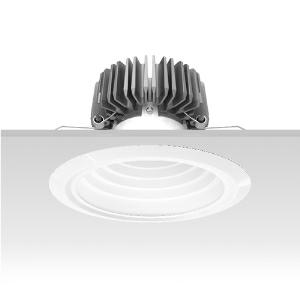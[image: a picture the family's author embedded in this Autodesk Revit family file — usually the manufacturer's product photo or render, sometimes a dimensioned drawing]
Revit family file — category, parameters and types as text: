
# Revit family: 3f_filippi_-_3f_reno_bianco_ampio_3f_filippi_-_30621_a01025_-_3f_reno_200_wh_2000-840_wide___vt_wh_48a5
name_source: partatom
category: Lighting Fixtures
units: mm (PartAtom-declared; Revit-internal decimal feet)

## family parameters
Cut with Voids When Loaded = No
Host = Face
Light Source = No
Part Type = Normal
Room Calculation Point = No
Round Connector Dimension = Use Diameter
Shared = No

## types (1)
- 3F Filippi - 3F Reno Bianco Ampio (1 x LED, 1884 lm, 20 W, 4000 K)
    Apparent Load = 20 VA
    Approval mark = CE
    CIE Flux Codes = 75 94 99 100 100
    Color Rendering = 80
    Color Temperature = 4000 K
    Control Gear = Electronic ballast
    Default Elevation = 1800 mm
    Description = ILLUMINOTECHNICAL
Luminous efficiency 100% (DLOR 100%, ULOR 0%).
Initial luminous flux of the luminaire 1884 lm.
Direct symmetric wide distribution.
Installation Interdistance Transv.D = 1.56 x hu - Long.D = 1.56 x hu.
Average luminance <3000 cd/m² for radial angles >65°.
Tabular UGR (CIE 117 - 4H-8H; S=0.25H; 70/50/20): RUG 20.8 - 20.6.
Beam angle: 74° - 74°.
Luminous efficacy 94 lm/W.
Lifetime (L90/B10): 30000 h. (tq+25°C)
Lifetime (L85/B10): 50000 h. (tq+25°C)
Lifetime (L70/B10): 80000 h. (tq+25°C)
Sudden decreased luminous flux after 50000 hours: 0% (C0).
Photobiological safety in compliance with IEC/TR 62778: RG0 risk exempt, (IEC 62471).
In compliance with IEC/EN 62722-2-1 - IEC/EN 62717 standards.

SOURCE
Compact LED module 2000/840.
Energy efficiency class (UE 2019/2020 - UE 2019/2015): D.
CIE 13.3 Colour rendering index: CRI >80 (R9 <50%).
IES TM-30 Fidelity Index: Rf = 84 Rg = 95.
CCT nominal colour temperature 4000 K.
Colour initial tolerance (MacAdam): SDCM 3.
Zhaga Book 3 compliant.

MECHANICAL
Passive heat dissipator in die-casting aluminium, oversized, for optimum thermal management of the LED module.
Parabolic element with graduated/concentric rings in white polycarbonate.
Transparent external lens with glossy and satin differentiated surfaces, with a cooling and anti-insect system in methacrylate (PMMA).
Fastening spring clips in stainless steel.
Dimensions: diameter 226 mm, height 146 mm. Weight 1.06 kg.
IP44 protection degree for exposed part, IP20 for recessed part.
Mechanical strength to impacts IK06 (1 joule).
Glow-wire test resistance 650°C.

ELECTRICAL
Wiring on a separate unit.
Halogen Free electronic wiring 230V-50/60Hz, power factor 0.95, THD <25%, constant output current, SELV, class II, 1 driver.
Power of the luminaire 20 W.
ENEC - CE.
SAFE FLICKER: PstLM=<1 and SVM=<0.4 (IEC TR 61547-1 and IEC TR 63158), to ensure a more comfortable and safe light.
Luminaire compliant with EN 60598-2-22 for power supply from a centralised emergency system CPSS (Central Power Supply System), not incorporated in the luminaire - high risk areas excluded. The default power and flux are 100% in AC and 100% in DC.
Ambient temperature from 0°C to +25°C.
Temperature class T6 max 85°C.
Relative humidity UR: <85%.

INSTALLATION
Pull-up recessed fitting.
False ceiling carving: 200 mm.
All accessories dedicated to this product are available on the Catalog and on our website www.3F-Filippi.com.

ACCESSORIES
A01025 - VT transparent glass, tempered, not flammable, locked and in line with the trim, in white polycarbonate.

APPLICATIONS
Environments: architectural, commercial, exhibition areas, transit areas, corridors, shops, display windows, service areas.
In false ceilings with narrow voids.

WARNING
Luminaire designed for disposal/recycling at end-of-life.
Replaceable (LED only) light source by a professional. Replaceable control gear by a professional.
    Height = 0 mm  [stored 0 ft]
    Lamp = 1 x LED
    Lamp Light Flux = 1884 lm
    Lamp Power = 20 W
    Lamp count = 1
    Length = 226 mm
    Lifetime = 50000 h
    Luminous efficacy = 94 lm/W
    Manufacturer = 3F Filippi
    ModVariant = No
    Model = 3F Filippi - 30621+A01025 - 3F Reno 200 WH 2000-840 WIDE + VT WH
    Mounting Place = Ceiling
    Mounting Type = Recessed
    Number of Poles = 1
    OnlyDefault = Yes
    Power Factor = 1
    Product Name = 3F Filippi - 3F Reno Bianco Ampio
    Product group = recessed luminaire
    ProductGroupID = 4
    Protection Class = Protection class II
    Protection Degree = IP 20
    RLX_Detail_Level = 1
    RLX_Emergency_Light_Flux = 0 lm
    RLX_Emergency_Type = 0
    RLX_Emergency_Type_DB = No
    RlxData = <blob elided: 96933 chars, md5=dfd1f9fd>
    Socket = socket
    Standby Power = 0 W
    System Light Flux = 1884 lm
    System Power = 20 W
    Type Comments = Product without accessories
    Type Image = 3ffilippi_3f_reno_200_wh__a01025.jpg
    URL = http://relux.com
    VarID = ---
    Voltage = 0 V
    Weight = 0.00 kg
    Width = 0 mm  [stored 0 ft]

note: [stored X ft] marks values corroborated as IEEE doubles in the binary element streams (Revit-internal decimal feet)

## geometry (parser evidence)
native form markers: Blend x4, Sweep x11
no freeform markers — native parametric forms only
